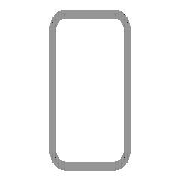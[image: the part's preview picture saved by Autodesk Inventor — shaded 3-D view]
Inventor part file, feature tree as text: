
AUTODESK INVENTOR PART (.ipt)
format: ipt  version: 2025 (Build 290162010, 162A)  size: 148,992 bytes
history: native  units: mm (DEFAULTED — no unit token found)
features: other x4, plane x3, split x2, sketch x1
ambient origin geometry x8: Origin, YZ Plane, XZ Plane, XY Plane, X Axis, Y Axis, Z Axis, Center Point
bodies: Solid1 (feature_tree), Body (feature_tree)
feature tree (10):
  parser-record x1  (decoder bookkeeping rows leaked as tree rows — omitted from the tree; the rows remain in map.json)
  other  "Driven Length"
  other  "Start Plane"
  other  "End Plane"
  plane  "Work Plane4"
  split  "Split1"
  plane  "Work Plane5"
  split  "Split2"
  sketch  "Sketch3"  dims[d3=1740.0mm d4=0.0mm d7=6.0mm d9=40.0mm d11=80.0mm d12=3.0mm d13=-0.0mm d14=1740.0mm d15=20.0mm d16=40.0mm d17=90.0deg d18=1740.0mm]
  plane  "Work Plane3"
